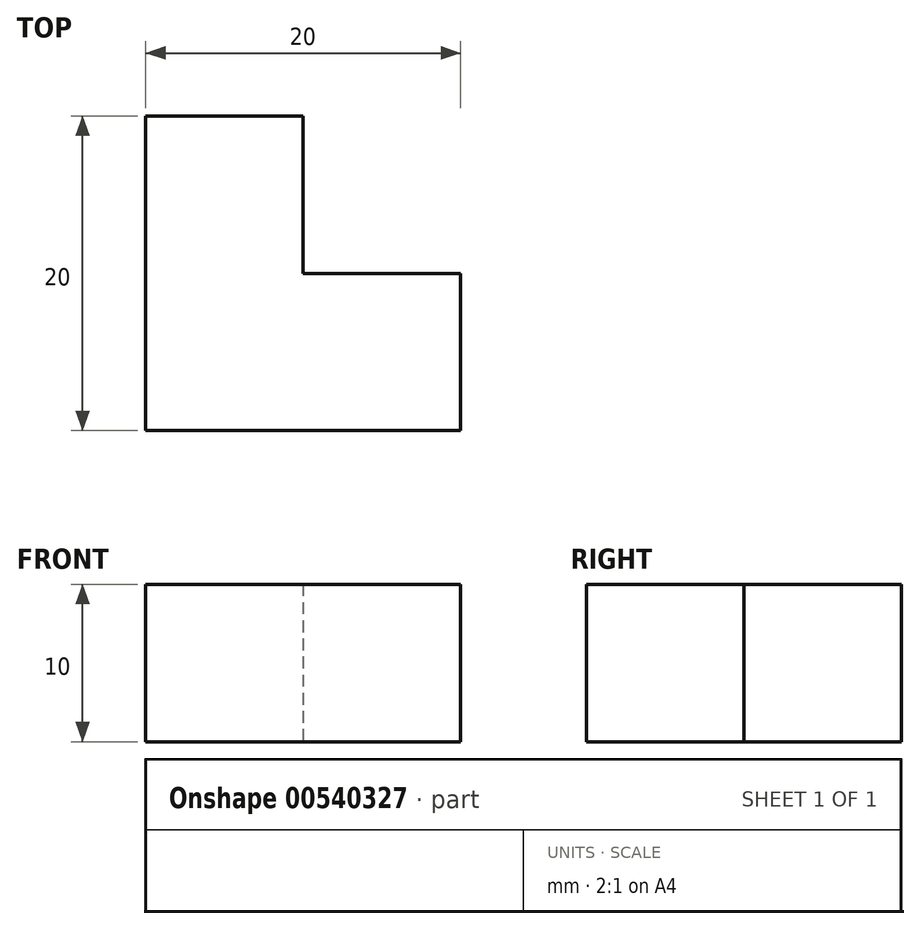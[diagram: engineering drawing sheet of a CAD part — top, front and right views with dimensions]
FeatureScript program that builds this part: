
annotation { "Feature Type Name" : "Feature", "Feature Type Description" : "" }
export const myFeature = defineFeature(function(context is Context, id is Id, definition is map)
    precondition{}
    {
        {
            var Q0;
            Q0=qCreatedBy(makeId("Top.planeOp"),FACE);
            var sketch = newSketch(context, id + "F0", { "sketchPlane" : qUnion([Q0])});
            skLineSegment(sketch, "E0", {"start": v(0, 0) * mm, "end": v(-20, 0) * mm});
            skLineSegment(sketch, "E1", {"start": v(-20, 0) * mm, "end": v(-20, 20) * mm});
            skLineSegment(sketch, "E2", {"start": v(-20, 20) * mm, "end": v(-10, 20) * mm});
            skLineSegment(sketch, "E3", {"start": v(-10, 20) * mm, "end": v(-10, 10) * mm});
            skLineSegment(sketch, "E4", {"start": v(-10, 10) * mm, "end": v(0, 10) * mm});
            skLineSegment(sketch, "E5", {"start": v(0, 10) * mm, "end": v(0, 0) * mm});
            skSolve(sketch);
        }
        {
            var Q0;
            Q0=makeQuery(id+"F0.imprint","IMPRINT",FACE,{"disambiguationData":[TD([[makeQuery(id+"F0.imprint","IMPRINT",EDGE,{"derivedFrom":sQuery(id+"F0.wireOp",EDGE,"E0")}),-1.0]])]});
            extrude(context, id + "F1", {"entities" : qUnion([Q0]), "depth" : 10 * mm, "offsetDistance" : 25 * mm});
        }
    });
